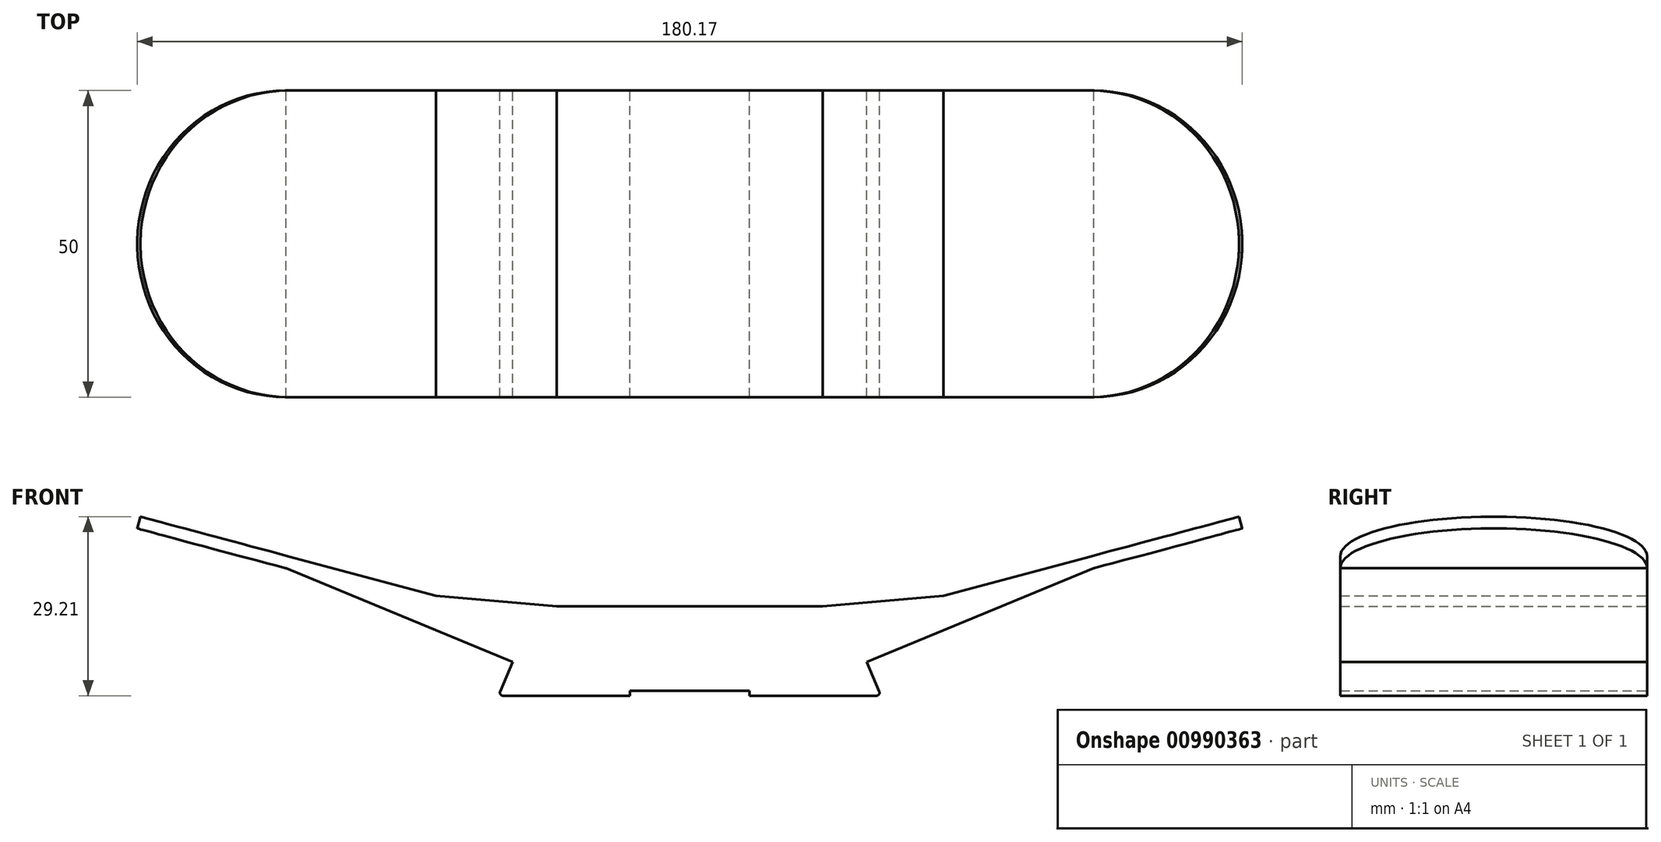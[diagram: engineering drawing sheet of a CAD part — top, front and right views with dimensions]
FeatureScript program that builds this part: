
annotation { "Feature Type Name" : "Feature", "Feature Type Description" : "" }
export const myFeature = defineFeature(function(context is Context, id is Id, definition is map)
    precondition{}
    {
        {
            var Q0;
            Q0=qCreatedBy(makeId("Front.planeOp"),FACE);
            var sketch = newSketch(context, id + "F0", { "sketchPlane" : qUnion([Q0])});
            skLineSegment(sketch, "E0", {"start": v(26.7, -11.58) * mm, "end": v(28.75, -6.78) * mm});
            skArc(sketch, "E1.filletArc", {"start": v(26.7, -11.58) * mm, "mid": v(26.74, -12.05) * mm, "end": v(27.15, -12.28) * mm});
            skLineSegment(sketch, "E2", {"start": v(27.15, -12.28) * mm, "end": v(47.85, -12.28) * mm});
            skLineSegment(sketch, "E3", {"start": v(47.85, -12.28) * mm, "end": v(47.85, -11.48) * mm});
            skLineSegment(sketch, "E4", {"start": v(28.75, -6.78) * mm, "end": v(35.82, 0.3) * mm});
            skLineSegment(sketch, "E5", {"start": v(35.82, 0.3) * mm, "end": v(15.9, 2.04) * mm});
            skLineSegment(sketch, "E6", {"start": v(15.9, 2.04) * mm, "end": v(-32.4, 14.98) * mm});
            skLineSegment(sketch, "E7.0", {"start": v(16.24, 4.02) * mm, "end": v(-31.89, 16.91) * mm});
            skLineSegment(sketch, "E7.4", {"start": v(35.9, 2.3) * mm, "end": v(16.24, 4.02) * mm});
            skArc(sketch, "E8", {"start": v(-31.89, 16.91) * mm, "mid": v(-33.1, 16.2) * mm, "end": v(-32.4, 14.98) * mm});
            skLineSegment(sketch, "E9", {"start": v(47.85, -11.48) * mm, "end": v(57.6, -11.48) * mm});
            skLineSegment(sketch, "E10", {"start": v(35.9, 2.3) * mm, "end": v(57.6, 2.3) * mm});
            skLineSegment(sketch, "E11", {"start": v(28.75, -6.78) * mm, "end": v(-8.25, 8.5) * mm});
            skLineSegment(sketch, "E12", {"start": v(57.6, 2.3) * mm, "end": v(57.6, -11.48) * mm});
            skSolve(sketch);
        }
        {
            var Q0;
            Q0=makeQuery(id+"F0.imprint","IMPRINT",FACE,{"disambiguationData":[TD([[makeQuery(id+"F0.imprint","IMPRINT",EDGE,{"derivedFrom":sQuery(id+"F0.wireOp",EDGE,"E0")}),-1.0]])]});
            var Q1;
            Q1=makeQuery(id+"F0.imprint","IMPRINT",FACE,{"disambiguationData":[TD([[makeQuery(id+"F0.imprint","IMPRINT",EDGE,{"derivedFrom":sQuery(id+"F0.wireOp",EDGE,"E4")}),1.0]])]});
            extrude(context, id + "F1", {"entities" : qUnion([Q0, Q1]), "depth" : 50 * mm, "offsetDistance" : 25 * mm});
        }
        {
            var Q0;
            Q0=makeQuery(id+"F1.opExtrude","SWEPT_FACE",FACE,{"disambiguationData":[OSD([sQuery(id+"F0.wireOp",EDGE,"E7.0")])]});
            var sketch = newSketch(context, id + "F2", { "sketchPlane" : qUnion([Q0])});
            skLineSegment(sketch, "E13", {"start": v(-10.26, -50) * mm, "end": v(-47.18, -50) * mm});
            skLineSegment(sketch, "E14", {"start": v(-47.18, -50) * mm, "end": v(-47.18, 0) * mm});
            skLineSegment(sketch, "E15", {"start": v(-47.18, 0) * mm, "end": v(-10.26, 0) * mm});
            skArc(sketch, "E16", {"start": v(-10.26, 0) * mm, "mid": v(-35.26, -25) * mm, "end": v(-10.26, -50) * mm});
            skSolve(sketch);
        }
        {
            var Q0;
            {var subQ0=sQuery(id+"F2.wireOp",EDGE,"E13");var subQ1=sQuery(id+"F0.wireOp",EDGE,"E7.0");var subQ2=makeQuery(id+"F1.opExtrude","SWEPT_EDGE",EDGE,{"disambiguationData":[OSD([subQ1,sQuery(id+"F0.wireOp",EDGE,"E8")])]});var subQ3=makeQuery(id+"F2.imprint","INTERSECT",VERTEX,{"derivedFrom":[subQ2,subQ0]});Q0=makeQuery(id+"F2.imprint","IMPRINT",FACE,{"disambiguationData":[TD([[makeQuery(id+"F2.imprint","IMPRINT",EDGE,{"disambiguationData":[TD([[subQ3,1.0]])],"derivedFrom":subQ0}),-1.0]])]});}
            var Q1;
            {var subQ0=sQuery(id+"F2.wireOp",EDGE,"E15");var subQ1=sQuery(id+"F0.wireOp",EDGE,"E7.0");var subQ4=sQuery(id+"F2.wireOp",EDGE,"E16");var subQ5=makeQuery(id+"F2.imprint","INTERSECT",VERTEX,{"derivedFrom":[makeQuery(id+"F1.opExtrude","CAP_EDGE",EDGE,{"disambiguationData":[OSD([subQ1])],"isStart":true}),subQ0,subQ4]});Q1=makeQuery(id+"F2.imprint","IMPRINT",FACE,{"disambiguationData":[TD([[makeQuery(id+"F2.imprint","IMPRINT",EDGE,{"disambiguationData":[TD([[subQ5,-1.0]])],"derivedFrom":subQ0}),1.0]])]});}
            var Q2;
            {var subQ6=sQuery(id+"F2.wireOp",EDGE,"E14");Q2=makeQuery(id+"F2.imprint","IMPRINT",FACE,{"disambiguationData":[TD([[makeQuery(id+"F2.imprint","IMPRINT",EDGE,{"derivedFrom":subQ6}),-1.0]])]});}
            extrude(context, id + "F3", {"entities" : qUnion([Q0, Q1, Q2]), "operationType" : NewBodyOperationType.REMOVE, "oppositeDirection" : true, "depth" : 4.4 * mm, "offsetDistance" : 25 * mm});
        }
        {
            var Q0;
            Q0=makeQuery(id+"F1.opExtrude","SWEPT_BODY",BODY,{"disambiguationData":[OSD([sQuery(id+"F0.wireOp",EDGE,"E0"),sQuery(id+"F0.wireOp",EDGE,"E1.filletArc"),sQuery(id+"F0.wireOp",EDGE,"E2"),sQuery(id+"F0.wireOp",EDGE,"E3"),sQuery(id+"F0.wireOp",EDGE,"E6"),sQuery(id+"F0.wireOp",EDGE,"E7.0"),sQuery(id+"F0.wireOp",EDGE,"E7.4"),sQuery(id+"F0.wireOp",EDGE,"E8"),sQuery(id+"F0.wireOp",EDGE,"E9"),sQuery(id+"F0.wireOp",EDGE,"E10"),sQuery(id+"F0.wireOp",EDGE,"E11"),sQuery(id+"F0.wireOp",EDGE,"E12")])]});
            var Q1;
            Q1=makeQuery(id+"F1.opExtrude","SWEPT_FACE",FACE,{"disambiguationData":[OSD([sQuery(id+"F0.wireOp",EDGE,"E12")])]});
            mirror(context, id + "F4", {"operationType" : NewBodyOperationType.ADD, "entities" : qUnion([Q0]), "mirrorPlane" : qUnion([Q1])});
        }
    });
